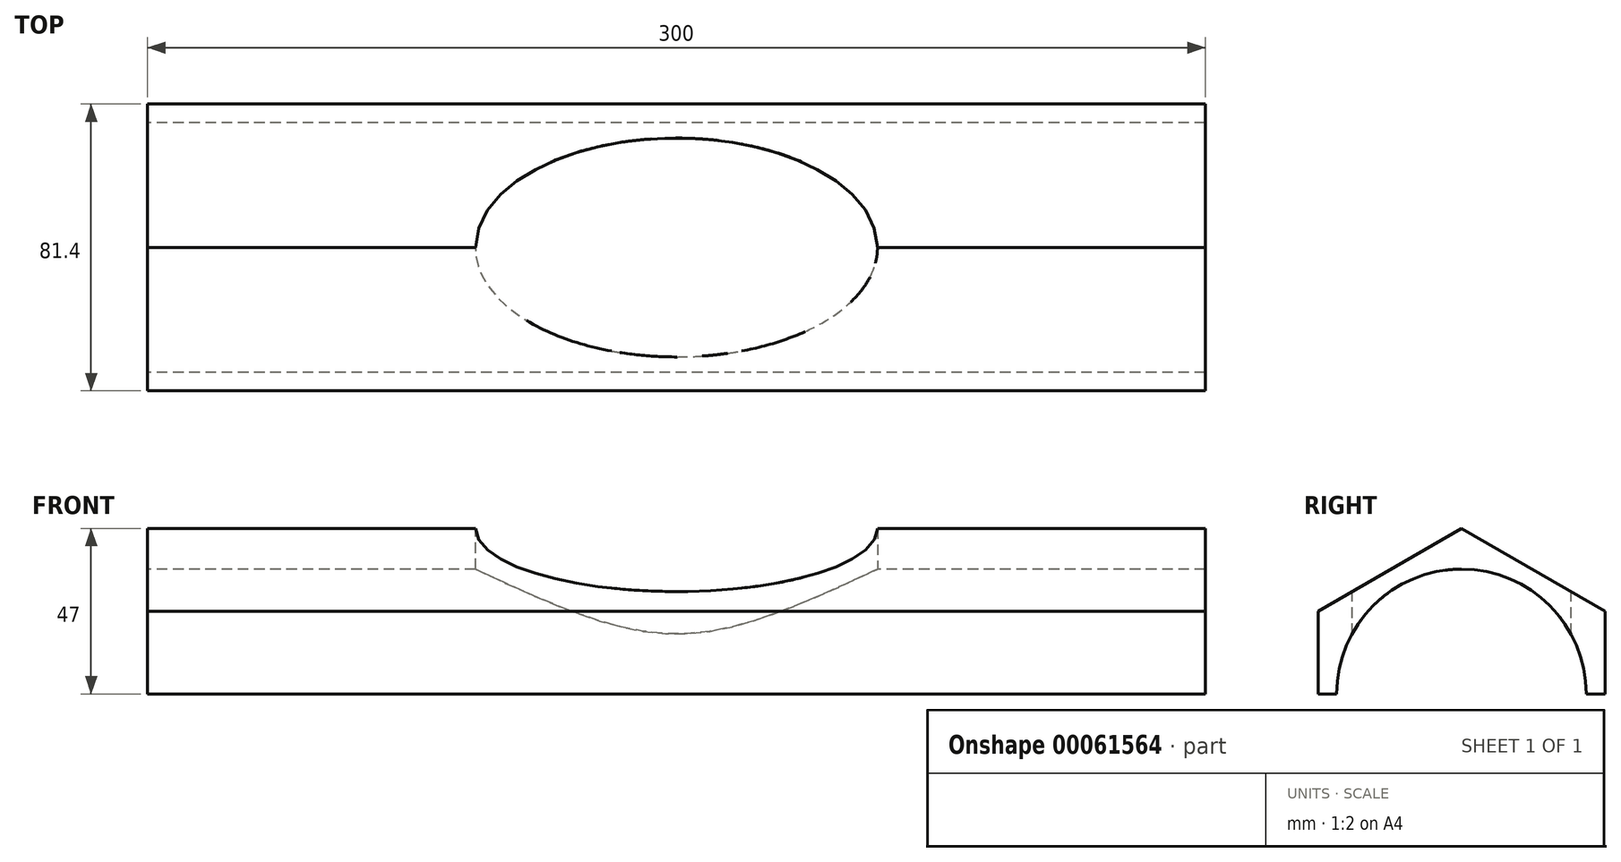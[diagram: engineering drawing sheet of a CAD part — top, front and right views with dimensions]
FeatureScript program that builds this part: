
annotation { "Feature Type Name" : "Feature", "Feature Type Description" : "" }
export const myFeature = defineFeature(function(context is Context, id is Id, definition is map)
    precondition{}
    {
        {
            var Q0;
            Q0=qCreatedBy(makeId("Right.planeOp"),FACE);
            var sketch = newSketch(context, id + "F0", { "sketchPlane" : qUnion([Q0])});
            skArc(sketch, "E0", {"start": v(35.4, 0) * mm, "mid": v(0, 35.4) * mm, "end": v(-35.4, 0) * mm});
            skArc(sketch, "E1.cCircle", {"start": v(40.7, 0) * mm, "mid": v(0, 40.7) * mm, "end": v(-40.7, 0) * mm, "construction": true});
            skLineSegment(sketch, "E1.0", {"start": v(40.7, 23.5) * mm, "end": v(40.7, 0) * mm});
            skLineSegment(sketch, "E1.3", {"start": v(-40.7, 0) * mm, "end": v(-40.7, 23.5) * mm});
            skLineSegment(sketch, "E1.4", {"start": v(-40.7, 23.5) * mm, "end": v(0, 47) * mm});
            skLineSegment(sketch, "E1.5", {"start": v(0, 47) * mm, "end": v(40.7, 23.5) * mm});
            skPoint(sketch, "E1.0.midPoint", {"position": v(40.7, 0) * mm});
            skLineSegment(sketch, "E2", {"start": v(-40.7, 0) * mm, "end": v(-35.4, 0) * mm});
            skLineSegment(sketch, "E3.trimOffspring", {"start": v(35.4, 0) * mm, "end": v(40.7, 0) * mm});
            skPoint(sketch, "E4.orphan", {"position": v(-40.7, -23.5) * mm});
            skPoint(sketch, "E5.orphan", {"position": v(40.7, -23.5) * mm});
            skSolve(sketch);
        }
        {
            var Q0;
            Q0=makeQuery(id+"F0.imprint","IMPRINT",FACE,{"disambiguationData":[TD([[makeQuery(id+"F0.imprint","IMPRINT",EDGE,{"derivedFrom":sQuery(id+"F0.wireOp",EDGE,"E0")}),-1.0]])]});
            extrude(context, id + "F1", {"entities" : qUnion([Q0]), "endBound" : BoundingType.SYMMETRIC, "depth" : 300 * mm});
        }
        {
            var Q0;
            Q0=qCreatedBy(makeId("Top.planeOp"),FACE);
            var sketch = newSketch(context, id + "F2", { "sketchPlane" : qUnion([Q0])});
            skEllipse(sketch, "E6", {"center": v(0, 0) * mm, "majorRadius": 57.03 * mm, "minorRadius": 31.06 * mm, "majorAxis": v(1, 0)});
            skSolve(sketch);
        }
        {
            var Q0;
            Q0=makeQuery(id+"F2.imprint","IMPRINT",FACE,{"disambiguationData":[TD([[makeQuery(id+"F2.imprint","IMPRINT",EDGE,{"derivedFrom":sQuery(id+"F2.wireOp",EDGE,"E6")}),1.0]])]});
            var Q1;
            Q1=sQuery(id+"F2.wireOp",EDGE,"E6");
            extrude(context, id + "F3", {"entities" : qUnion([Q0]), "operationType" : NewBodyOperationType.REMOVE, "surfaceEntities" : qUnion([Q1]), "endBound" : BoundingType.THROUGH_ALL, "depth" : 25 * mm});
        }
    });
